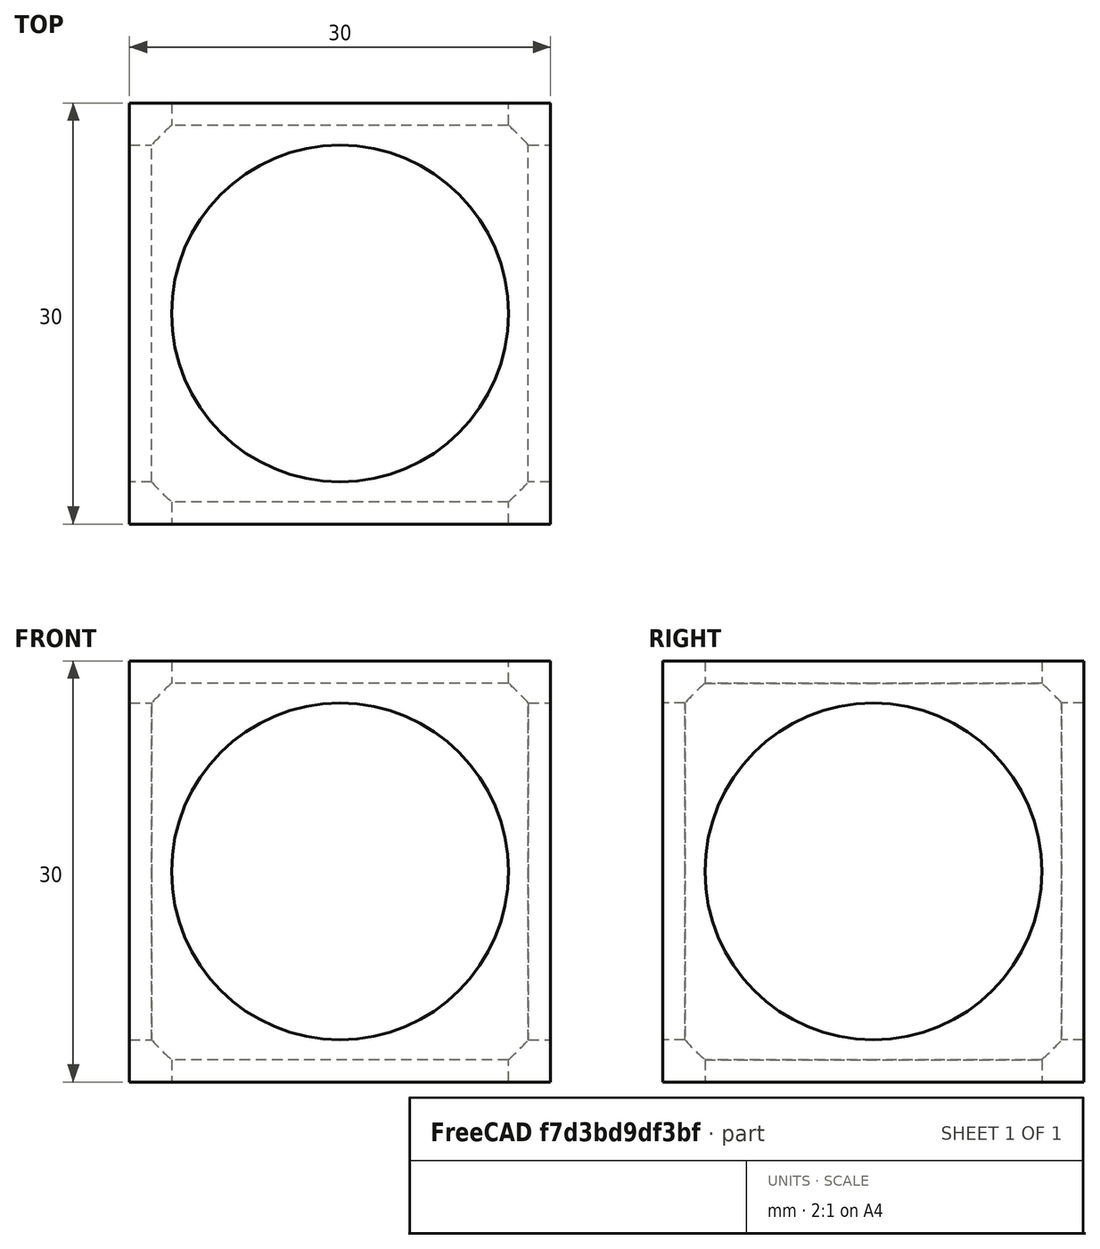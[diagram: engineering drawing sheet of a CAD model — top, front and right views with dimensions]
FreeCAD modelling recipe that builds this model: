
FCSTD DOCUMENT  (FreeCAD 0.21R33694 (Git))
Label: prodriguez_repte3
License: All rights reserved
LicenseURL: https://en.wikipedia.org/wiki/All_rights_reserved
objects: Part::Cylinder×3, Part::Sphere×2, Part::Cut×2, Part::Box×1, Part::MultiFuse×1
note: 9 computed .brp shape members not serialized (recipe doc carries the construction recipe); baked Part::Feature solids carry a one-line shape summary decoded from their .brp

FEATURE [Part::Box] Box  label="Cub"
  AttacherType = Attacher::AttachEngine3D
  Height = 30
  Length = 30
  Width = 30
FEATURE [Part::Cylinder] Cylinder001  label="Cilindre001"
  Angle = 360
  AttacherType = Attacher::AttachEngine3D
  FirstAngle = 0
  Height = 35
  Placement = pos=(15,-2.5,15) rot=(-1,0,0;1.5708rad)
  Radius = 12
  SecondAngle = 0
  expr: .Placement.Base.x = 15
  expr: .Placement.Base.y = -2.5
  expr: .Placement.Base.z = 15
  expr: .Placement.Rotation.Roll = -90
FEATURE [Part::Cylinder] Cylinder002  label="Cilindre002"
  Angle = 360
  AttacherType = Attacher::AttachEngine3D
  FirstAngle = 0
  Height = 35
  Placement = pos=(15,15,-2.5) rot=(0,0,1;0rad)
  Radius = 12
  SecondAngle = 0
  expr: .Placement.Base.x = 15
  expr: .Placement.Base.y = 15
  expr: .Placement.Base.z = -2.5
  expr: .Placement.Rotation.Pitch = 0
  expr: .Placement.Rotation.Roll = 0
  expr: .Placement.Rotation.Yaw = 0
FEATURE [Part::Cylinder] Cylinder003  label="Cilindre003"
  Angle = 360
  AttacherType = Attacher::AttachEngine3D
  FirstAngle = 0
  Height = 35
  Placement = pos=(32.5,15,15) rot=(0.57735,-0.57735,-0.57735;2.0944rad)
  Radius = 12
  SecondAngle = 0
  expr: .Placement.Base.x = 32.5
  expr: .Placement.Base.y = 15
  expr: .Placement.Base.z = 15
  expr: .Placement.Rotation.Pitch = 0
  expr: .Placement.Rotation.Roll = 90
  expr: .Placement.Rotation.Yaw = -90
FEATURE [Part::MultiFuse] Fusion
  Shapes = -> [Cylinder001,Cylinder002,Cylinder003]
FEATURE [Part::Sphere] Sphere  label="Esfera"
  Angle1 = -90
  Angle2 = 90
  Angle3 = 360
  AttacherType = Attacher::AttachEngine3D
  Placement = pos=(15,15,15) rot=(0,0,1;0rad)
  Radius = 12
  expr: .Placement.Base.x = 15
  expr: .Placement.Base.y = 15
  expr: .Placement.Base.z = 15
FEATURE [Part::Cut] Cut
  Base = -> Box
  Tool = -> Fusion
FEATURE [Part::Sphere] Sphere001  label="Esfera001"
  Angle1 = -90
  Angle2 = 90
  Angle3 = 360
  AttacherType = Attacher::AttachEngine3D
  Placement = pos=(15,15,15) rot=(0,0,1;0rad)
  Radius = 18
  expr: .Placement.Base.x = 15
  expr: .Placement.Base.y = 15
  expr: .Placement.Base.z = 15
FEATURE [Part::Cut] Cut001
  Base = -> Cut
  Tool = -> Sphere001
